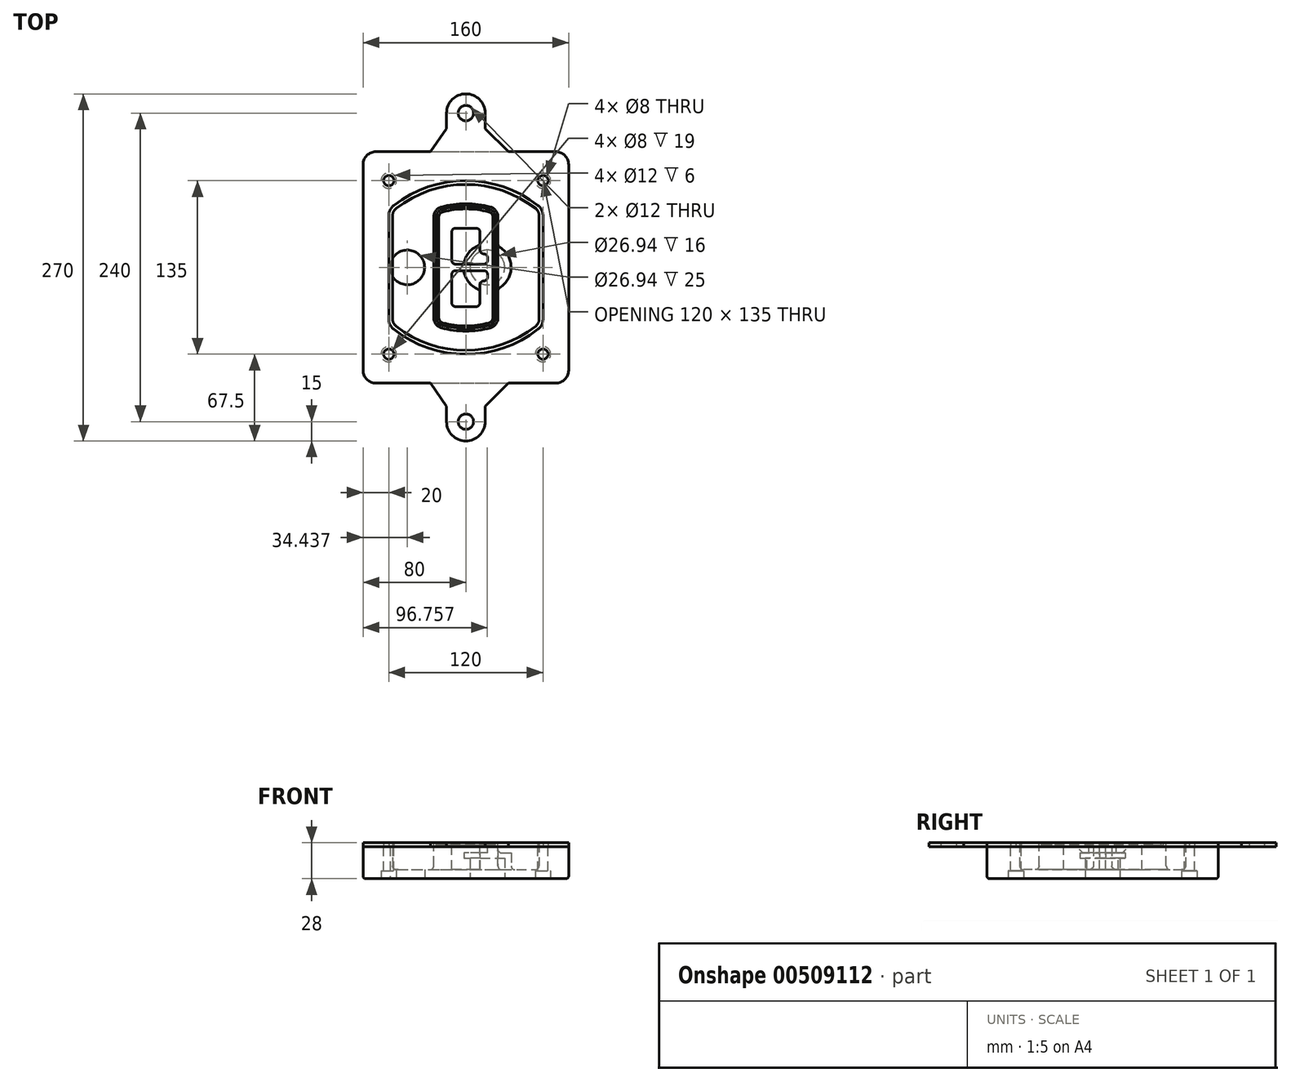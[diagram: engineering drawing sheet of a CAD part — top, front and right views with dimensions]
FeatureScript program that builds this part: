
annotation { "Feature Type Name" : "Feature", "Feature Type Description" : "" }
export const myFeature = defineFeature(function(context is Context, id is Id, definition is map)
    precondition{}
    {
        {
            var Q0;
            Q0=qCreatedBy(makeId("Top.planeOp"),FACE);
            var sketch = newSketch(context, id + "F0", { "sketchPlane" : qUnion([Q0])});
            skPoint(sketch, "E0.rect.middle", {"position": v(0, 0) * mm});
            skLineSegment(sketch, "E1.bottom", {"start": v(-70, -90) * mm, "end": v(70, -90) * mm});
            skLineSegment(sketch, "E1.top", {"start": v(-70, 90) * mm, "end": v(70, 90) * mm});
            skLineSegment(sketch, "E1.left", {"start": v(-80, -80) * mm, "end": v(-80, 80) * mm});
            skLineSegment(sketch, "E1.right", {"start": v(80, -80) * mm, "end": v(80, 80) * mm});
            skLineSegment(sketch, "E2", {"start": v(-80, 90) * mm, "end": v(80, -90) * mm, "construction": true});
            skLineSegment(sketch, "E3", {"start": v(80, 90) * mm, "end": v(-80, -90) * mm, "construction": true});
            skCircle(sketch, "E4", {"center": v(-60, 67.5) * mm, "radius": 4 * mm});
            skCircle(sketch, "E5", {"center": v(60, 67.5) * mm, "radius": 4 * mm});
            skCircle(sketch, "E6", {"center": v(60, -67.5) * mm, "radius": 4 * mm});
            skCircle(sketch, "E7", {"center": v(-60, -67.5) * mm, "radius": 4 * mm});
            skLineSegment(sketch, "E8", {"start": v(-60, 67.5) * mm, "end": v(60, 67.5) * mm, "construction": true});
            skLineSegment(sketch, "E9", {"start": v(60, 67.5) * mm, "end": v(60, -67.5) * mm, "construction": true});
            skLineSegment(sketch, "E10", {"start": v(60, -67.5) * mm, "end": v(-60, -67.5) * mm, "construction": true});
            skLineSegment(sketch, "E11", {"start": v(-60, -67.5) * mm, "end": v(-60, 67.5) * mm, "construction": true});
            skLineSegment(sketch, "E12", {"start": v(-60, 40.3) * mm, "end": v(-60, -40.3) * mm});
            skLineSegment(sketch, "E13", {"start": v(60, 40.3) * mm, "end": v(60, -40.3) * mm});
            skArc(sketch, "E14", {"start": v(56.15, 48.18) * mm, "mid": v(0, 67.5) * mm, "end": v(-56.15, 48.18) * mm});
            skArc(sketch, "E15", {"start": v(-56.15, -48.18) * mm, "mid": v(0, -67.5) * mm, "end": v(56.15, -48.18) * mm});
            skLineSegment(sketch, "E16", {"start": v(-60, 0) * mm, "end": v(60, 0) * mm, "construction": true});
            skPoint(sketch, "E17.visualSharp", {"position": v(-60, -45) * mm});
            skArc(sketch, "E17.filletArc", {"start": v(-60, -40.3) * mm, "mid": v(-58.99, -44.68) * mm, "end": v(-56.15, -48.18) * mm});
            skPoint(sketch, "E18.visualSharp", {"position": v(-60, 45) * mm});
            skArc(sketch, "E18.filletArc", {"start": v(-56.15, 48.18) * mm, "mid": v(-58.99, 44.68) * mm, "end": v(-60, 40.3) * mm});
            skPoint(sketch, "E19.visualSharp", {"position": v(60, 45) * mm});
            skArc(sketch, "E19.filletArc", {"start": v(60, 40.3) * mm, "mid": v(58.99, 44.68) * mm, "end": v(56.15, 48.18) * mm});
            skPoint(sketch, "E20.visualSharp", {"position": v(60, -45) * mm});
            skArc(sketch, "E20.filletArc", {"start": v(56.15, -48.18) * mm, "mid": v(58.99, -44.68) * mm, "end": v(60, -40.3) * mm});
            skPoint(sketch, "E21.visualSharp", {"position": v(-80, 90) * mm});
            skArc(sketch, "E21.filletArc", {"start": v(-70, 90) * mm, "mid": v(-77.07, 87.07) * mm, "end": v(-80, 80) * mm});
            skPoint(sketch, "E22.visualSharp", {"position": v(80, 90) * mm});
            skArc(sketch, "E22.filletArc", {"start": v(80, 80) * mm, "mid": v(77.07, 87.07) * mm, "end": v(70, 90) * mm});
            skPoint(sketch, "E23.visualSharp", {"position": v(80, -90) * mm});
            skArc(sketch, "E23.filletArc", {"start": v(70, -90) * mm, "mid": v(77.07, -87.07) * mm, "end": v(80, -80) * mm});
            skPoint(sketch, "E24.visualSharp", {"position": v(-80, -90) * mm});
            skArc(sketch, "E24.filletArc", {"start": v(-80, -80) * mm, "mid": v(-77.07, -87.07) * mm, "end": v(-70, -90) * mm});
            skArc(sketch, "E25.0", {"start": v(57, 40.3) * mm, "mid": v(56.3, 43.36) * mm, "end": v(54.3, 45.81) * mm});
            skLineSegment(sketch, "E25.1", {"start": v(57, 40.3) * mm, "end": v(57, -40.3) * mm});
            skArc(sketch, "E25.2", {"start": v(54.3, -45.81) * mm, "mid": v(56.3, -43.36) * mm, "end": v(57, -40.3) * mm});
            skArc(sketch, "E25.3", {"start": v(-54.3, -45.81) * mm, "mid": v(0, -64.5) * mm, "end": v(54.3, -45.81) * mm});
            skArc(sketch, "E25.4", {"start": v(-57, -40.3) * mm, "mid": v(-56.3, -43.36) * mm, "end": v(-54.3, -45.81) * mm});
            skArc(sketch, "E25.5", {"start": v(54.3, 45.81) * mm, "mid": v(0, 64.5) * mm, "end": v(-54.3, 45.81) * mm});
            skLineSegment(sketch, "E25.6", {"start": v(-57, 40.3) * mm, "end": v(-57, -40.3) * mm});
            skArc(sketch, "E25.7", {"start": v(-54.3, 45.81) * mm, "mid": v(-56.3, 43.36) * mm, "end": v(-57, 40.3) * mm});
            skArc(sketch, "E26.0", {"start": v(-58.62, 51.33) * mm, "mid": v(-62.58, 46.43) * mm, "end": v(-64, 40.3) * mm});
            skArc(sketch, "E26.1", {"start": v(58.62, 51.33) * mm, "mid": v(0, 71.5) * mm, "end": v(-58.62, 51.33) * mm});
            skArc(sketch, "E26.2", {"start": v(64, 40.3) * mm, "mid": v(62.58, 46.43) * mm, "end": v(58.62, 51.33) * mm});
            skLineSegment(sketch, "E26.3", {"start": v(64, 40.3) * mm, "end": v(64, -40.3) * mm});
            skArc(sketch, "E26.4", {"start": v(58.62, -51.33) * mm, "mid": v(62.58, -46.43) * mm, "end": v(64, -40.3) * mm});
            skLineSegment(sketch, "E26.5", {"start": v(-64, 40.3) * mm, "end": v(-64, -40.3) * mm});
            skArc(sketch, "E26.6", {"start": v(-58.62, -51.33) * mm, "mid": v(0, -71.5) * mm, "end": v(58.62, -51.33) * mm});
            skArc(sketch, "E26.7", {"start": v(-64, -40.3) * mm, "mid": v(-62.58, -46.43) * mm, "end": v(-58.62, -51.33) * mm});
            skSolve(sketch);
        }
        {
            var Q0;
            Q0=makeQuery(id+"F0.imprint","IMPRINT",FACE,{"disambiguationData":[TD([[makeQuery(id+"F0.imprint","IMPRINT",EDGE,{"derivedFrom":sQuery(id+"F0.wireOp",EDGE,"E1.bottom")}),1.0]])]});
            var Q1;
            Q1=makeQuery(id+"F0.imprint","IMPRINT",FACE,{"disambiguationData":[TD([[makeQuery(id+"F0.imprint","IMPRINT",EDGE,{"derivedFrom":sQuery(id+"F0.wireOp",EDGE,"E12")}),1.0]])]});
            var Q2;
            Q2=makeQuery(id+"F0.imprint","IMPRINT",FACE,{"disambiguationData":[TD([[makeQuery(id+"F0.imprint","IMPRINT",EDGE,{"derivedFrom":sQuery(id+"F0.wireOp",EDGE,"E25.0")}),1.0]])]});
            var Q3;
            Q3=makeQuery(id+"F0.imprint","IMPRINT",FACE,{"disambiguationData":[TD([[makeQuery(id+"F0.imprint","IMPRINT",EDGE,{"derivedFrom":sQuery(id+"F0.wireOp",EDGE,"E12")}),-1.0]])]});
            extrude(context, id + "F1", {"entities" : qUnion([Q0, Q1, Q2, Q3]), "oppositeDirection" : true, "depth" : 25 * mm});
        }
        {
            var Q0;
            Q0=makeQuery(id+"F0.imprint","IMPRINT",FACE,{"disambiguationData":[TD([[makeQuery(id+"F0.imprint","IMPRINT",EDGE,{"derivedFrom":sQuery(id+"F0.wireOp",EDGE,"E12")}),1.0]])]});
            extrude(context, id + "F2", {"entities" : qUnion([Q0]), "operationType" : NewBodyOperationType.ADD, "depth" : 3 * mm});
        }
        {
            var Q0;
            Q0=makeQuery(id+"F0.imprint","IMPRINT",FACE,{"disambiguationData":[TD([[makeQuery(id+"F0.imprint","IMPRINT",EDGE,{"derivedFrom":sQuery(id+"F0.wireOp",EDGE,"E25.0")}),1.0]])]});
            extrude(context, id + "F3", {"entities" : qUnion([Q0]), "operationType" : NewBodyOperationType.REMOVE, "oppositeDirection" : true, "depth" : 18 * mm});
        }
        {
            var Q0;
            Q0=makeQuery(id+"F2.opExtrude","CAP_FACE",FACE,{"disambiguationData":[OSD([sQuery(id+"F0.wireOp",EDGE,"E12"),sQuery(id+"F0.wireOp",EDGE,"E13"),sQuery(id+"F0.wireOp",EDGE,"E14"),sQuery(id+"F0.wireOp",EDGE,"E15"),sQuery(id+"F0.wireOp",EDGE,"E17.filletArc"),sQuery(id+"F0.wireOp",EDGE,"E18.filletArc"),sQuery(id+"F0.wireOp",EDGE,"E19.filletArc"),sQuery(id+"F0.wireOp",EDGE,"E20.filletArc"),sQuery(id+"F0.wireOp",EDGE,"E25.0"),sQuery(id+"F0.wireOp",EDGE,"E25.1"),sQuery(id+"F0.wireOp",EDGE,"E25.2"),sQuery(id+"F0.wireOp",EDGE,"E25.3"),sQuery(id+"F0.wireOp",EDGE,"E25.4"),sQuery(id+"F0.wireOp",EDGE,"E25.5"),sQuery(id+"F0.wireOp",EDGE,"E25.6"),sQuery(id+"F0.wireOp",EDGE,"E25.7")])],"isStart":false});
            var sketch = newSketch(context, id + "F4", { "sketchPlane" : qUnion([Q0])});
            skArc(sketch, "E27.0", {"start": v(-19.08, -46.97) * mm, "mid": v(0, -49.5) * mm, "end": v(19.08, -46.97) * mm});
            skArc(sketch, "E28.0", {"start": v(19.08, 46.97) * mm, "mid": v(0, 49.5) * mm, "end": v(-19.08, 46.97) * mm});
            skLineSegment(sketch, "E29", {"start": v(-25, 39.25) * mm, "end": v(-25, -39.25) * mm});
            skLineSegment(sketch, "E30", {"start": v(25, 39.25) * mm, "end": v(25, -39.25) * mm});
            skLineSegment(sketch, "E31", {"start": v(-25, 45.1) * mm, "end": v(25, 45.1) * mm, "construction": true});
            skLineSegment(sketch, "E32", {"start": v(-25, -45.1) * mm, "end": v(25, -45.1) * mm, "construction": true});
            skPoint(sketch, "E33.visualSharp", {"position": v(-25, 45.1) * mm});
            skArc(sketch, "E33.filletArc", {"start": v(-19.08, 46.97) * mm, "mid": v(-23.35, 44.11) * mm, "end": v(-25, 39.25) * mm});
            skPoint(sketch, "E34.visualSharp", {"position": v(25, 45.1) * mm});
            skArc(sketch, "E34.filletArc", {"start": v(25, 39.25) * mm, "mid": v(23.35, 44.11) * mm, "end": v(19.08, 46.97) * mm});
            skPoint(sketch, "E35.visualSharp", {"position": v(25, -45.1) * mm});
            skArc(sketch, "E35.filletArc", {"start": v(19.08, -46.97) * mm, "mid": v(23.35, -44.11) * mm, "end": v(25, -39.25) * mm});
            skPoint(sketch, "E36.visualSharp", {"position": v(-25, -45.1) * mm});
            skArc(sketch, "E36.filletArc", {"start": v(-25, -39.25) * mm, "mid": v(-23.35, -44.11) * mm, "end": v(-19.08, -46.97) * mm});
            skArc(sketch, "E37.0", {"start": v(54.3, 45.81) * mm, "mid": v(0, 64.5) * mm, "end": v(-54.3, 45.81) * mm});
            skArc(sketch, "E37.1", {"start": v(-54.3, 45.81) * mm, "mid": v(-56.3, 43.36) * mm, "end": v(-57, 40.3) * mm});
            skLineSegment(sketch, "E37.2", {"start": v(-57, 40.3) * mm, "end": v(-57, -40.3) * mm});
            skArc(sketch, "E37.3", {"start": v(-57, -40.3) * mm, "mid": v(-56.3, -43.36) * mm, "end": v(-54.3, -45.81) * mm});
            skArc(sketch, "E37.4", {"start": v(-54.3, -45.81) * mm, "mid": v(0, -64.5) * mm, "end": v(54.3, -45.81) * mm});
            skArc(sketch, "E37.5", {"start": v(54.3, -45.81) * mm, "mid": v(56.3, -43.36) * mm, "end": v(57, -40.3) * mm});
            skLineSegment(sketch, "E37.6", {"start": v(57, 40.3) * mm, "end": v(57, -40.3) * mm});
            skArc(sketch, "E37.7", {"start": v(57, 40.3) * mm, "mid": v(56.3, 43.36) * mm, "end": v(54.3, 45.81) * mm});
            skLineSegment(sketch, "E38.0", {"start": v(23, 39.25) * mm, "end": v(23, -39.25) * mm});
            skArc(sketch, "E38.1", {"start": v(18.56, -45.04) * mm, "mid": v(21.76, -42.9) * mm, "end": v(23, -39.25) * mm});
            skArc(sketch, "E38.2", {"start": v(-18.56, -45.04) * mm, "mid": v(0, -47.5) * mm, "end": v(18.56, -45.04) * mm});
            skArc(sketch, "E38.3", {"start": v(-23, -39.25) * mm, "mid": v(-21.76, -42.9) * mm, "end": v(-18.56, -45.04) * mm});
            skLineSegment(sketch, "E38.4", {"start": v(-23, 39.25) * mm, "end": v(-23, -39.25) * mm});
            skArc(sketch, "E38.5", {"start": v(23, 39.25) * mm, "mid": v(21.76, 42.9) * mm, "end": v(18.56, 45.04) * mm});
            skArc(sketch, "E38.6", {"start": v(-18.56, 45.04) * mm, "mid": v(-21.76, 42.9) * mm, "end": v(-23, 39.25) * mm});
            skArc(sketch, "E38.7", {"start": v(18.56, 45.04) * mm, "mid": v(0, 47.5) * mm, "end": v(-18.56, 45.04) * mm});
            skArc(sketch, "E39.0", {"start": v(21, 39.25) * mm, "mid": v(20.18, 41.68) * mm, "end": v(18.04, 43.1) * mm});
            skLineSegment(sketch, "E39.1", {"start": v(21, 39.25) * mm, "end": v(21, -39.25) * mm});
            skArc(sketch, "E39.2", {"start": v(18.04, -43.1) * mm, "mid": v(20.18, -41.68) * mm, "end": v(21, -39.25) * mm});
            skArc(sketch, "E39.3", {"start": v(-18.04, -43.1) * mm, "mid": v(0, -45.5) * mm, "end": v(18.04, -43.1) * mm});
            skArc(sketch, "E39.4", {"start": v(-21, -39.25) * mm, "mid": v(-20.18, -41.68) * mm, "end": v(-18.04, -43.1) * mm});
            skArc(sketch, "E39.5", {"start": v(18.04, 43.1) * mm, "mid": v(0, 45.5) * mm, "end": v(-18.04, 43.1) * mm});
            skLineSegment(sketch, "E39.6", {"start": v(-21, 39.25) * mm, "end": v(-21, -39.25) * mm});
            skArc(sketch, "E39.7", {"start": v(-18.04, 43.1) * mm, "mid": v(-20.18, 41.68) * mm, "end": v(-21, 39.25) * mm});
            skLineSegment(sketch, "E40", {"start": v(-25, 0) * mm, "end": v(25, 0) * mm, "construction": true});
            skLineSegment(sketch, "E41", {"start": v(-11, 5.5) * mm, "end": v(-11, 27.5) * mm});
            skLineSegment(sketch, "E42", {"start": v(-8, 30.5) * mm, "end": v(8, 30.5) * mm});
            skLineSegment(sketch, "E43", {"start": v(11, 27.5) * mm, "end": v(11, 13.5) * mm});
            skLineSegment(sketch, "E44", {"start": v(14, 10.5) * mm, "end": v(14, 10.5) * mm});
            skLineSegment(sketch, "E45", {"start": v(17, 7.5) * mm, "end": v(17, 5.5) * mm});
            skLineSegment(sketch, "E46", {"start": v(14, 2.5) * mm, "end": v(-8, 2.5) * mm});
            skPoint(sketch, "E47.visualSharp", {"position": v(-11, 30.5) * mm});
            skArc(sketch, "E47.filletArc", {"start": v(-8, 30.5) * mm, "mid": v(-10.12, 29.62) * mm, "end": v(-11, 27.5) * mm});
            skPoint(sketch, "E48.visualSharp", {"position": v(11, 30.5) * mm});
            skArc(sketch, "E48.filletArc", {"start": v(11, 27.5) * mm, "mid": v(10.12, 29.62) * mm, "end": v(8, 30.5) * mm});
            skPoint(sketch, "E49.visualSharp", {"position": v(11, 10.5) * mm});
            skArc(sketch, "E49.filletArc", {"start": v(11, 13.5) * mm, "mid": v(11.88, 11.38) * mm, "end": v(14, 10.5) * mm});
            skPoint(sketch, "E50.visualSharp", {"position": v(17, 10.5) * mm});
            skArc(sketch, "E50.filletArc", {"start": v(17, 7.5) * mm, "mid": v(16.12, 9.62) * mm, "end": v(14, 10.5) * mm});
            skPoint(sketch, "E51.visualSharp", {"position": v(17, 2.5) * mm});
            skArc(sketch, "E51.filletArc", {"start": v(14, 2.5) * mm, "mid": v(16.12, 3.38) * mm, "end": v(17, 5.5) * mm});
            skPoint(sketch, "E52.visualSharp", {"position": v(-11, 2.5) * mm});
            skArc(sketch, "E52.filletArc", {"start": v(-11, 5.5) * mm, "mid": v(-10.12, 3.38) * mm, "end": v(-8, 2.5) * mm});
            skLineSegment(sketch, "E53.0.MirrorCS", {"start": v(14, -2.5) * mm, "end": v(-8, -2.5) * mm});
            skArc(sketch, "E54.0.MirrorCS", {"start": v(-11, -5.5) * mm, "mid": v(-10.12, -3.38) * mm, "end": v(-8, -2.5) * mm});
            skLineSegment(sketch, "E55.0.MirrorCS", {"start": v(-11, -5.5) * mm, "end": v(-11, -27.5) * mm});
            skArc(sketch, "E56.0.MirrorCS", {"start": v(-8, -30.5) * mm, "mid": v(-10.12, -29.62) * mm, "end": v(-11, -27.5) * mm});
            skLineSegment(sketch, "E57.0.MirrorCS", {"start": v(-8, -30.5) * mm, "end": v(8, -30.5) * mm});
            skArc(sketch, "E58.0.MirrorCS", {"start": v(11, -27.5) * mm, "mid": v(10.12, -29.62) * mm, "end": v(8, -30.5) * mm});
            skLineSegment(sketch, "E59.0.MirrorCS", {"start": v(11, -27.5) * mm, "end": v(11, -13.5) * mm});
            skArc(sketch, "E60.0.MirrorCS", {"start": v(11, -13.5) * mm, "mid": v(11.88, -11.38) * mm, "end": v(14, -10.5) * mm});
            skArc(sketch, "E61.0.MirrorCS", {"start": v(17, -7.5) * mm, "mid": v(16.12, -9.62) * mm, "end": v(14, -10.5) * mm});
            skLineSegment(sketch, "E62.0.MirrorCS", {"start": v(17, -7.5) * mm, "end": v(17, -5.5) * mm});
            skArc(sketch, "E63.0.MirrorCS", {"start": v(14, -2.5) * mm, "mid": v(16.12, -3.38) * mm, "end": v(17, -5.5) * mm});
            skSolve(sketch);
        }
        {
            var Q0;
            Q0=makeQuery(id+"F4.imprint","IMPRINT",FACE,{"disambiguationData":[TD([[makeQuery(id+"F4.imprint","IMPRINT",EDGE,{"derivedFrom":sQuery(id+"F4.wireOp",EDGE,"E27.0")}),1.0]])]});
            var Q1;
            Q1=makeQuery(id+"F4.imprint","IMPRINT",FACE,{"disambiguationData":[TD([[makeQuery(id+"F4.imprint","IMPRINT",EDGE,{"derivedFrom":sQuery(id+"F4.wireOp",EDGE,"E38.0")}),-1.0]])]});
            var Q2;
            Q2=makeQuery(id+"F4.imprint","IMPRINT",FACE,{"disambiguationData":[TD([[makeQuery(id+"F4.imprint","IMPRINT",EDGE,{"derivedFrom":sQuery(id+"F4.wireOp",EDGE,"E39.0")}),1.0]])]});
            extrude(context, id + "F5", {"entities" : qUnion([Q0, Q1, Q2]), "operationType" : NewBodyOperationType.ADD, "endBound" : BoundingType.UP_TO_NEXT, "oppositeDirection" : true, "depth" : 25 * mm});
        }
        {
            var Q0;
            Q0=makeQuery(id+"F4.imprint","IMPRINT",FACE,{"disambiguationData":[TD([[makeQuery(id+"F4.imprint","IMPRINT",EDGE,{"derivedFrom":sQuery(id+"F4.wireOp",EDGE,"E38.0")}),-1.0]])]});
            extrude(context, id + "F6", {"entities" : qUnion([Q0]), "operationType" : NewBodyOperationType.REMOVE, "oppositeDirection" : true, "depth" : 2 * mm});
        }
        {
            var Q0;
            Q0=makeQuery(id+"F1.opExtrude","CAP_FACE",FACE,{"disambiguationData":[OSD([sQuery(id+"F0.wireOp",EDGE,"E1.bottom"),sQuery(id+"F0.wireOp",EDGE,"E1.top"),sQuery(id+"F0.wireOp",EDGE,"E1.left"),sQuery(id+"F0.wireOp",EDGE,"E1.right"),sQuery(id+"F0.wireOp",EDGE,"E4"),sQuery(id+"F0.wireOp",EDGE,"E5"),sQuery(id+"F0.wireOp",EDGE,"E6"),sQuery(id+"F0.wireOp",EDGE,"E7"),sQuery(id+"F0.wireOp",EDGE,"E21.filletArc"),sQuery(id+"F0.wireOp",EDGE,"E22.filletArc"),sQuery(id+"F0.wireOp",EDGE,"E23.filletArc"),sQuery(id+"F0.wireOp",EDGE,"E24.filletArc")])],"isStart":false});
            var sketch = newSketch(context, id + "F7", { "sketchPlane" : qUnion([Q0])});
            skCircle(sketch, "E64", {"center": v(16.76, 0) * mm, "radius": 13.47 * mm});
            skCircle(sketch, "E65", {"center": v(-45.56, 0) * mm, "radius": 13.47 * mm});
            skLineSegment(sketch, "E66", {"start": v(80, 0) * mm, "end": v(-80, 0) * mm});
            skCircle(sketch, "E67", {"center": v(16.76, 0) * mm, "radius": 18.47 * mm});
            skCircle(sketch, "E68", {"center": v(60, -67.5) * mm, "radius": 6 * mm});
            skCircle(sketch, "E69", {"center": v(-60, -67.5) * mm, "radius": 6 * mm});
            skCircle(sketch, "E70", {"center": v(-60, 67.5) * mm, "radius": 6 * mm});
            skCircle(sketch, "E71", {"center": v(60, 67.5) * mm, "radius": 6 * mm});
            skSolve(sketch);
        }
        {
            var Q0;
            {var subQ1=sQuery(id+"F7.wireOp",EDGE,"E66");var subQ4=sQuery(id+"F7.wireOp",EDGE,"E64");var subQ6=makeQuery(id+"F7.imprint","INTERSECT",VERTEX,{"disambiguationData":[OD(0.0)],"derivedFrom":[subQ4,subQ1]});Q0=makeQuery(id+"F7.imprint","IMPRINT",FACE,{"disambiguationData":[TD([[makeQuery(id+"F7.imprint","IMPRINT",EDGE,{"disambiguationData":[TD([[subQ6,-1.0]])],"derivedFrom":subQ4}),-1.0]])]});}
            var Q1;
            {var subQ0=sQuery(id+"F7.wireOp",EDGE,"E66");var subQ1=sQuery(id+"F7.wireOp",EDGE,"E64");var subQ3=makeQuery(id+"F7.imprint","INTERSECT",VERTEX,{"disambiguationData":[OD(0.0)],"derivedFrom":[subQ1,subQ0]});Q1=makeQuery(id+"F7.imprint","IMPRINT",FACE,{"disambiguationData":[TD([[makeQuery(id+"F7.imprint","IMPRINT",EDGE,{"disambiguationData":[TD([[subQ3,-1.0]])],"derivedFrom":subQ1}),1.0]])]});}
            var Q2;
            {var subQ0=sQuery(id+"F7.wireOp",EDGE,"E66");var subQ1=sQuery(id+"F7.wireOp",EDGE,"E64");var subQ3=makeQuery(id+"F7.imprint","INTERSECT",VERTEX,{"disambiguationData":[OD(0.0)],"derivedFrom":[subQ1,subQ0]});Q2=makeQuery(id+"F7.imprint","IMPRINT",FACE,{"disambiguationData":[TD([[makeQuery(id+"F7.imprint","IMPRINT",EDGE,{"disambiguationData":[TD([[subQ3,1.0]])],"derivedFrom":subQ1}),1.0]])]});}
            var Q3;
            {var subQ1=sQuery(id+"F7.wireOp",EDGE,"E66");var subQ4=sQuery(id+"F7.wireOp",EDGE,"E64");var subQ6=makeQuery(id+"F7.imprint","INTERSECT",VERTEX,{"disambiguationData":[OD(0.0)],"derivedFrom":[subQ4,subQ1]});Q3=makeQuery(id+"F7.imprint","IMPRINT",FACE,{"disambiguationData":[TD([[makeQuery(id+"F7.imprint","IMPRINT",EDGE,{"disambiguationData":[TD([[subQ6,1.0]])],"derivedFrom":subQ4}),-1.0]])]});}
            extrude(context, id + "F8", {"entities" : qUnion([Q0, Q1, Q2, Q3]), "operationType" : NewBodyOperationType.ADD, "oppositeDirection" : true, "depth" : 20 * mm});
        }
        {
            var Q0;
            {var subQ0=sQuery(id+"F7.wireOp",EDGE,"E66");var subQ1=sQuery(id+"F7.wireOp",EDGE,"E64");var subQ3=makeQuery(id+"F7.imprint","INTERSECT",VERTEX,{"disambiguationData":[OD(0.0)],"derivedFrom":[subQ1,subQ0]});Q0=makeQuery(id+"F7.imprint","IMPRINT",FACE,{"disambiguationData":[TD([[makeQuery(id+"F7.imprint","IMPRINT",EDGE,{"disambiguationData":[TD([[subQ3,-1.0]])],"derivedFrom":subQ1}),1.0]])]});}
            var Q1;
            {var subQ0=sQuery(id+"F7.wireOp",EDGE,"E66");var subQ1=sQuery(id+"F7.wireOp",EDGE,"E64");var subQ3=makeQuery(id+"F7.imprint","INTERSECT",VERTEX,{"disambiguationData":[OD(0.0)],"derivedFrom":[subQ1,subQ0]});Q1=makeQuery(id+"F7.imprint","IMPRINT",FACE,{"disambiguationData":[TD([[makeQuery(id+"F7.imprint","IMPRINT",EDGE,{"disambiguationData":[TD([[subQ3,1.0]])],"derivedFrom":subQ1}),1.0]])]});}
            extrude(context, id + "F9", {"entities" : qUnion([Q0, Q1]), "operationType" : NewBodyOperationType.REMOVE, "oppositeDirection" : true, "depth" : 16 * mm});
        }
        {
            var Q0;
            {var subQ0=sQuery(id+"F7.wireOp",EDGE,"E66");var subQ1=sQuery(id+"F7.wireOp",EDGE,"E65");var subQ3=makeQuery(id+"F7.imprint","INTERSECT",VERTEX,{"disambiguationData":[OD(0.0)],"derivedFrom":[subQ1,subQ0]});Q0=makeQuery(id+"F7.imprint","IMPRINT",FACE,{"disambiguationData":[TD([[makeQuery(id+"F7.imprint","IMPRINT",EDGE,{"disambiguationData":[TD([[subQ3,-1.0]])],"derivedFrom":subQ1}),1.0]])]});}
            var Q1;
            {var subQ0=sQuery(id+"F7.wireOp",EDGE,"E66");var subQ1=sQuery(id+"F7.wireOp",EDGE,"E65");var subQ3=makeQuery(id+"F7.imprint","INTERSECT",VERTEX,{"disambiguationData":[OD(0.0)],"derivedFrom":[subQ1,subQ0]});Q1=makeQuery(id+"F7.imprint","IMPRINT",FACE,{"disambiguationData":[TD([[makeQuery(id+"F7.imprint","IMPRINT",EDGE,{"disambiguationData":[TD([[subQ3,1.0]])],"derivedFrom":subQ1}),1.0]])]});}
            extrude(context, id + "F10", {"entities" : qUnion([Q0, Q1]), "operationType" : NewBodyOperationType.REMOVE, "oppositeDirection" : true, "depth" : 25 * mm});
        }
        {
            var Q0;
            Q0=makeQuery(id+"F7.imprint","IMPRINT",FACE,{"disambiguationData":[TD([[makeQuery(id+"F7.imprint","IMPRINT",EDGE,{"derivedFrom":sQuery(id+"F7.wireOp",EDGE,"E68")}),1.0]])]});
            var Q1;
            Q1=makeQuery(id+"F7.imprint","IMPRINT",FACE,{"disambiguationData":[TD([[makeQuery(id+"F7.imprint","IMPRINT",EDGE,{"derivedFrom":makeQuery(id+"F1.opExtrude","CAP_EDGE",EDGE,{"disambiguationData":[OSD([sQuery(id+"F0.wireOp",EDGE,"E5")])],"isStart":false})}),-1.0]])]});
            var Q2;
            Q2=makeQuery(id+"F7.imprint","IMPRINT",FACE,{"disambiguationData":[TD([[makeQuery(id+"F7.imprint","IMPRINT",EDGE,{"derivedFrom":sQuery(id+"F7.wireOp",EDGE,"E69")}),1.0]])]});
            var Q3;
            Q3=makeQuery(id+"F7.imprint","IMPRINT",FACE,{"disambiguationData":[TD([[makeQuery(id+"F7.imprint","IMPRINT",EDGE,{"derivedFrom":makeQuery(id+"F1.opExtrude","CAP_EDGE",EDGE,{"disambiguationData":[OSD([sQuery(id+"F0.wireOp",EDGE,"E4")])],"isStart":false})}),-1.0]])]});
            var Q4;
            Q4=makeQuery(id+"F7.imprint","IMPRINT",FACE,{"disambiguationData":[TD([[makeQuery(id+"F7.imprint","IMPRINT",EDGE,{"derivedFrom":sQuery(id+"F7.wireOp",EDGE,"E70")}),1.0]])]});
            var Q5;
            Q5=makeQuery(id+"F7.imprint","IMPRINT",FACE,{"disambiguationData":[TD([[makeQuery(id+"F7.imprint","IMPRINT",EDGE,{"derivedFrom":makeQuery(id+"F1.opExtrude","CAP_EDGE",EDGE,{"disambiguationData":[OSD([sQuery(id+"F0.wireOp",EDGE,"E7")])],"isStart":false})}),-1.0]])]});
            var Q6;
            Q6=makeQuery(id+"F7.imprint","IMPRINT",FACE,{"disambiguationData":[TD([[makeQuery(id+"F7.imprint","IMPRINT",EDGE,{"derivedFrom":sQuery(id+"F7.wireOp",EDGE,"E71")}),1.0]])]});
            var Q7;
            Q7=makeQuery(id+"F7.imprint","IMPRINT",FACE,{"disambiguationData":[TD([[makeQuery(id+"F7.imprint","IMPRINT",EDGE,{"derivedFrom":makeQuery(id+"F1.opExtrude","CAP_EDGE",EDGE,{"disambiguationData":[OSD([sQuery(id+"F0.wireOp",EDGE,"E6")])],"isStart":false})}),-1.0]])]});
            extrude(context, id + "F11", {"entities" : qUnion([Q0, Q1, Q2, Q3, Q4, Q5, Q6, Q7]), "operationType" : NewBodyOperationType.REMOVE, "oppositeDirection" : true, "depth" : 6 * mm});
        }
        {
            var Q0;
            Q0=makeQuery(id+"F9.boolean.opBoolean","COPY",FACE,{"derivedFrom":makeQuery(id+"F9.opExtrude","CAP_FACE",FACE,{"disambiguationData":[OSD([sQuery(id+"F7.wireOp",EDGE,"E64")])],"isStart":false})});
            var sketch = newSketch(context, id + "F12", { "sketchPlane" : qUnion([Q0])});
            skArc(sketch, "E72.0", {"start": v(11, 17.55) * mm, "mid": v(2.57, 11.82) * mm, "end": v(-1.54, 2.5) * mm});
            skArc(sketch, "E72.1", {"start": v(-1.54, -2.5) * mm, "mid": v(2.57, -11.82) * mm, "end": v(11, -17.55) * mm});
            skLineSegment(sketch, "E73", {"start": v(-1.54, -2.5) * mm, "end": v(14, -2.5) * mm});
            skLineSegment(sketch, "E74.0", {"start": v(14, 2.5) * mm, "end": v(-1.54, 2.5) * mm});
            skArc(sketch, "E74.1", {"start": v(14, 2.5) * mm, "mid": v(16.12, 3.38) * mm, "end": v(17, 5.5) * mm});
            skLineSegment(sketch, "E74.2", {"start": v(17, 7.5) * mm, "end": v(17, 5.5) * mm});
            skArc(sketch, "E74.3", {"start": v(17, 7.5) * mm, "mid": v(16.12, 9.62) * mm, "end": v(14, 10.5) * mm});
            skArc(sketch, "E74.4", {"start": v(11, 13.5) * mm, "mid": v(11.88, 11.38) * mm, "end": v(14, 10.5) * mm});
            skLineSegment(sketch, "E74.5", {"start": v(11, 17.55) * mm, "end": v(11, 13.5) * mm});
            skLineSegment(sketch, "E74.7", {"start": v(14, -2.5) * mm, "end": v(-1.54, -2.5) * mm});
            skArc(sketch, "E74.8", {"start": v(14, -2.5) * mm, "mid": v(16.12, -3.38) * mm, "end": v(17, -5.5) * mm});
            skLineSegment(sketch, "E74.9", {"start": v(17, -7.5) * mm, "end": v(17, -5.5) * mm});
            skArc(sketch, "E74.10", {"start": v(17, -7.5) * mm, "mid": v(16.12, -9.62) * mm, "end": v(14, -10.5) * mm});
            skArc(sketch, "E74.11", {"start": v(11, -13.5) * mm, "mid": v(11.88, -11.38) * mm, "end": v(14, -10.5) * mm});
            skLineSegment(sketch, "E74.12", {"start": v(11, -17.55) * mm, "end": v(11, -13.5) * mm});
            skPoint(sketch, "E75.orphan", {"position": v(11, -27.5) * mm});
            skPoint(sketch, "E76.orphan", {"position": v(-8, -2.5) * mm});
            skPoint(sketch, "E77.orphan", {"position": v(-8, 2.5) * mm});
            skPoint(sketch, "E78.orphan", {"position": v(11, 27.5) * mm});
            skSolve(sketch);
        }
        {
            var Q0;
            {var subQ7=sQuery(id+"F12.wireOp",EDGE,"E72.0");var subQ14=sQuery(id+"F12.wireOp",EDGE,"E72.1");var subQ16=sQuery(id+"F12.wireOp",EDGE,"E74.1");var subQ18=sQuery(id+"F12.wireOp",EDGE,"E74.8");Q0=qUnion([makeQuery(id+"F12.imprint","IMPRINT",FACE,{"disambiguationData":[TD([[makeQuery(id+"F12.imprint","IMPRINT",EDGE,{"derivedFrom":subQ7}),1.0]])]}),makeQuery(id+"F12.imprint","IMPRINT",FACE,{"disambiguationData":[TD([[makeQuery(id+"F12.imprint","IMPRINT",EDGE,{"derivedFrom":subQ14}),1.0]])]}),makeQuery(id+"F12.imprint","IMPRINT",FACE,{"disambiguationData":[TD([[makeQuery(id+"F12.imprint","IMPRINT",EDGE,{"derivedFrom":subQ16}),1.0]])]}),makeQuery(id+"F12.imprint","IMPRINT",FACE,{"disambiguationData":[TD([[makeQuery(id+"F12.imprint","IMPRINT",EDGE,{"derivedFrom":subQ18}),-1.0]])]})]);}
            var Q1;
            Q1=makeQuery(id+"F5.boolean.opBoolean","SPLIT",FACE,{"disambiguationData":[TD([makeQuery(id+"F5.opExtrude","SWEPT_FACE",FACE,{"disambiguationData":[OSD([sQuery(id+"F4.wireOp",EDGE,"E41")])]})])],"derivedFrom":makeQuery(id+"F3.boolean.opBoolean","COPY",FACE,{"derivedFrom":makeQuery(id+"F3.opExtrude","CAP_FACE",FACE,{"disambiguationData":[OSD([sQuery(id+"F0.wireOp",EDGE,"E25.0"),sQuery(id+"F0.wireOp",EDGE,"E25.1"),sQuery(id+"F0.wireOp",EDGE,"E25.2"),sQuery(id+"F0.wireOp",EDGE,"E25.3"),sQuery(id+"F0.wireOp",EDGE,"E25.4"),sQuery(id+"F0.wireOp",EDGE,"E25.5"),sQuery(id+"F0.wireOp",EDGE,"E25.6"),sQuery(id+"F0.wireOp",EDGE,"E25.7")])],"isStart":false})})});
            extrude(context, id + "F13", {"entities" : qUnion([Q0]), "operationType" : NewBodyOperationType.REMOVE, "endBound" : BoundingType.UP_TO_SURFACE, "endBoundEntityFace" : qUnion([Q1]), "depth" : 25 * mm});
        }
        {
            var Q0;
            Q0=makeQuery(id+"F3.boolean.opBoolean","COPY",EDGE,{"derivedFrom":makeQuery(id+"F3.opExtrude","CAP_EDGE",EDGE,{"disambiguationData":[OSD([sQuery(id+"F0.wireOp",EDGE,"E25.6")])],"isStart":false})});
            var Q1;
            Q1=makeQuery(id+"F8.boolean.opBoolean","INTERSECT",EDGE,{"derivedFrom":[makeQuery(id+"F5.opExtrude","SWEPT_FACE",FACE,{"disambiguationData":[OSD([sQuery(id+"F4.wireOp",EDGE,"E30")])]}),makeQuery(id+"F8.opExtrude","CAP_FACE",FACE,{"disambiguationData":[OSD([sQuery(id+"F7.wireOp",EDGE,"E67")])],"isStart":false})]});
            var Q2;
            Q2=makeQuery(id+"F8.boolean.opBoolean","INTERSECT",EDGE,{"disambiguationData":[OD(1.0)],"derivedFrom":[makeQuery(id+"F5.opExtrude","SWEPT_FACE",FACE,{"disambiguationData":[OSD([sQuery(id+"F4.wireOp",EDGE,"E30")])]}),makeQuery(id+"F8.opExtrude","SWEPT_FACE",FACE,{"disambiguationData":[OSD([sQuery(id+"F7.wireOp",EDGE,"E67")])]})]});
            var Q3;
            {var subQ0=sQuery(id+"F4.wireOp",EDGE,"E30");Q3=makeQuery(id+"F8.boolean.opBoolean","SPLIT",EDGE,{"disambiguationData":[TD([makeQuery(id+"F5.opExtrude","SWEPT_FACE",FACE,{"disambiguationData":[OSD([sQuery(id+"F4.wireOp",EDGE,"E35.filletArc")])]})])],"derivedFrom":makeQuery(id+"F5.opExtrude","CAP_EDGE",EDGE,{"disambiguationData":[OSD([subQ0])],"isStart":false})});}
            var Q4;
            {var subQ0=sQuery(id+"F0.wireOp",EDGE,"E25.7");var subQ1=sQuery(id+"F0.wireOp",EDGE,"E25.1");var subQ2=sQuery(id+"F0.wireOp",EDGE,"E25.6");var subQ3=sQuery(id+"F0.wireOp",EDGE,"E25.5");var subQ4=sQuery(id+"F0.wireOp",EDGE,"E25.4");var subQ5=sQuery(id+"F0.wireOp",EDGE,"E25.0");var subQ6=sQuery(id+"F0.wireOp",EDGE,"E25.2");var subQ7=sQuery(id+"F0.wireOp",EDGE,"E25.3");Q4=makeQuery(id+"F8.boolean.opBoolean","INTERSECT",EDGE,{"derivedFrom":[makeQuery(id+"F5.boolean.opBoolean","SPLIT",FACE,{"disambiguationData":[TD([makeQuery(id+"F2.opExtrude","SWEPT_FACE",FACE,{"disambiguationData":[OSD([subQ5])]})])],"derivedFrom":makeQuery(id+"F3.boolean.opBoolean","COPY",FACE,{"derivedFrom":makeQuery(id+"F3.opExtrude","CAP_FACE",FACE,{"disambiguationData":[OSD([subQ5,subQ1,subQ6,subQ7,subQ4,subQ3,subQ2,subQ0])],"isStart":false})})}),makeQuery(id+"F8.opExtrude","SWEPT_FACE",FACE,{"disambiguationData":[OSD([sQuery(id+"F7.wireOp",EDGE,"E67")])]})]});}
            var Q5;
            Q5=makeQuery(id+"F8.boolean.opBoolean","INTERSECT",EDGE,{"disambiguationData":[OD(0.0)],"derivedFrom":[makeQuery(id+"F5.opExtrude","SWEPT_FACE",FACE,{"disambiguationData":[OSD([sQuery(id+"F4.wireOp",EDGE,"E30")])]}),makeQuery(id+"F8.opExtrude","SWEPT_FACE",FACE,{"disambiguationData":[OSD([sQuery(id+"F7.wireOp",EDGE,"E67")])]})]});
            fillet(context, id + "F14", {"entities" : qUnion([Q0, Q1, Q2, Q3, Q4, Q5]), "radius" : 3 * mm, "tangentPropagation" : true, "allowEdgeOverflow" : false});
        }
        {
            var Q0;
            Q0=makeQuery(id+"F1.opExtrude","CAP_EDGE",EDGE,{"disambiguationData":[OSD([sQuery(id+"F0.wireOp",EDGE,"E1.bottom")])],"isStart":false});
            fillet(context, id + "F15", {"entities" : qUnion([Q0]), "radius" : 2 * mm, "tangentPropagation" : true, "allowEdgeOverflow" : false});
        }
        {
            var Q0;
            {var subQ0=sQuery(id+"F0.wireOp",EDGE,"E21.filletArc");var subQ1=sQuery(id+"F0.wireOp",EDGE,"E7");var subQ2=sQuery(id+"F0.wireOp",EDGE,"E6");var subQ3=sQuery(id+"F0.wireOp",EDGE,"E5");var subQ4=sQuery(id+"F0.wireOp",EDGE,"E4");var subQ5=sQuery(id+"F0.wireOp",EDGE,"E22.filletArc");var subQ6=sQuery(id+"F0.wireOp",EDGE,"E1.bottom");var subQ7=sQuery(id+"F0.wireOp",EDGE,"E1.right");var subQ8=sQuery(id+"F0.wireOp",EDGE,"E1.top");var subQ9=sQuery(id+"F0.wireOp",EDGE,"E1.left");var subQ10=sQuery(id+"F0.wireOp",EDGE,"E23.filletArc");var subQ11=sQuery(id+"F0.wireOp",EDGE,"E24.filletArc");Q0=makeQuery(id+"F2.boolean.opBoolean","SPLIT",FACE,{"disambiguationData":[TD([makeQuery(id+"F1.opExtrude","SWEPT_FACE",FACE,{"disambiguationData":[OSD([subQ6])]})])],"derivedFrom":makeQuery(id+"F1.opExtrude","CAP_FACE",FACE,{"disambiguationData":[OSD([subQ6,subQ8,subQ9,subQ7,subQ4,subQ3,subQ2,subQ1,subQ0,subQ5,subQ10,subQ11])],"isStart":true})});}
            var sketch = newSketch(context, id + "F16", { "sketchPlane" : qUnion([Q0])});
            skLineSegment(sketch, "E79.0", {"start": v(-70, 90) * mm, "end": v(70, 90) * mm});
            skLineSegment(sketch, "E79.1", {"start": v(-80, -80) * mm, "end": v(-80, 80) * mm});
            skLineSegment(sketch, "E79.2", {"start": v(-70, -90) * mm, "end": v(70, -90) * mm});
            skLineSegment(sketch, "E79.3", {"start": v(80, -80) * mm, "end": v(80, 80) * mm});
            skArc(sketch, "E79.4", {"start": v(80, 80) * mm, "mid": v(77.07, 87.07) * mm, "end": v(70, 90) * mm});
            skArc(sketch, "E79.5", {"start": v(-70, 90) * mm, "mid": v(-77.07, 87.07) * mm, "end": v(-80, 80) * mm});
            skArc(sketch, "E79.6", {"start": v(-80, -80) * mm, "mid": v(-77.07, -87.07) * mm, "end": v(-70, -90) * mm});
            skArc(sketch, "E79.7", {"start": v(70, -90) * mm, "mid": v(77.07, -87.07) * mm, "end": v(80, -80) * mm});
            skCircle(sketch, "E79.8", {"center": v(-60, 67.5) * mm, "radius": 4 * mm});
            skCircle(sketch, "E79.9", {"center": v(60, 67.5) * mm, "radius": 4 * mm});
            skCircle(sketch, "E79.10", {"center": v(-60, -67.5) * mm, "radius": 4 * mm});
            skCircle(sketch, "E79.11", {"center": v(60, -67.5) * mm, "radius": 4 * mm});
            skLineSegment(sketch, "E79.12", {"start": v(-60, 40.3) * mm, "end": v(-60, -40.3) * mm});
            skArc(sketch, "E79.13", {"start": v(56.15, 48.18) * mm, "mid": v(0, 67.5) * mm, "end": v(-56.15, 48.18) * mm});
            skArc(sketch, "E79.14", {"start": v(-56.15, 48.18) * mm, "mid": v(-58.99, 44.68) * mm, "end": v(-60, 40.3) * mm});
            skArc(sketch, "E79.15", {"start": v(-56.15, -48.18) * mm, "mid": v(0, -67.5) * mm, "end": v(56.15, -48.18) * mm});
            skArc(sketch, "E79.16", {"start": v(-60, -40.3) * mm, "mid": v(-58.99, -44.68) * mm, "end": v(-56.15, -48.18) * mm});
            skLineSegment(sketch, "E79.17", {"start": v(60, 40.3) * mm, "end": v(60, -40.3) * mm});
            skArc(sketch, "E79.18", {"start": v(56.15, -48.18) * mm, "mid": v(58.99, -44.68) * mm, "end": v(60, -40.3) * mm});
            skArc(sketch, "E79.19", {"start": v(60, 40.3) * mm, "mid": v(58.99, 44.68) * mm, "end": v(56.15, 48.18) * mm});
            skLineSegment(sketch, "E80", {"start": v(0, 90) * mm, "end": v(0, 120) * mm, "construction": true});
            skPoint(sketch, "E80.endSnap0", {"position": v(0, 90) * mm});
            skLineSegment(sketch, "E81", {"start": v(-27.44, 90) * mm, "end": v(-15, 108) * mm});
            skLineSegment(sketch, "E82", {"start": v(-15, 108) * mm, "end": v(-15, 120) * mm});
            skLineSegment(sketch, "E83", {"start": v(33, 90) * mm, "end": v(15, 108) * mm});
            skLineSegment(sketch, "E84", {"start": v(15, 108) * mm, "end": v(15, 120) * mm});
            skArc(sketch, "E85", {"start": v(-15, 120) * mm, "mid": v(0, 135) * mm, "end": v(15, 120) * mm});
            skCircle(sketch, "E86", {"center": v(0, 120) * mm, "radius": 6 * mm});
            skLineSegment(sketch, "E87.MirrorCS", {"start": v(-70, 270) * mm, "end": v(70, 270) * mm});
            skLineSegment(sketch, "E88", {"start": v(80, 0) * mm, "end": v(-78.28, 0) * mm, "construction": true});
            skPoint(sketch, "E88.endSnap0", {"position": v(-80, 0) * mm});
            skCircle(sketch, "E89.MirrorC", {"center": v(0, -120) * mm, "radius": 6 * mm});
            skArc(sketch, "E90.MirrorCS", {"start": v(-15, -120) * mm, "mid": v(0, -135) * mm, "end": v(15, -120) * mm});
            skLineSegment(sketch, "E91.MirrorCS", {"start": v(15, -108) * mm, "end": v(15, -120) * mm});
            skLineSegment(sketch, "E92.MirrorCS", {"start": v(33, -90) * mm, "end": v(15, -108) * mm});
            skLineSegment(sketch, "E93.MirrorCS", {"start": v(-15, -108) * mm, "end": v(-15, -120) * mm});
            skLineSegment(sketch, "E94.MirrorCS", {"start": v(-27.44, -90) * mm, "end": v(-15, -108) * mm});
            skLineSegment(sketch, "E95.MirrorCS", {"start": v(0, -90) * mm, "end": v(0, -120) * mm, "construction": true});
            skSolve(sketch);
        }
        {
            var Q0;
            Q0 = qSketchRegion(id + "F16", true);
            var Q1;
            Q1=makeQuery(id+"F2.opExtrude","CAP_FACE",FACE,{"disambiguationData":[OSD([sQuery(id+"F0.wireOp",EDGE,"E12"),sQuery(id+"F0.wireOp",EDGE,"E13"),sQuery(id+"F0.wireOp",EDGE,"E14"),sQuery(id+"F0.wireOp",EDGE,"E15"),sQuery(id+"F0.wireOp",EDGE,"E17.filletArc"),sQuery(id+"F0.wireOp",EDGE,"E18.filletArc"),sQuery(id+"F0.wireOp",EDGE,"E19.filletArc"),sQuery(id+"F0.wireOp",EDGE,"E20.filletArc"),sQuery(id+"F0.wireOp",EDGE,"E25.0"),sQuery(id+"F0.wireOp",EDGE,"E25.1"),sQuery(id+"F0.wireOp",EDGE,"E25.2"),sQuery(id+"F0.wireOp",EDGE,"E25.3"),sQuery(id+"F0.wireOp",EDGE,"E25.4"),sQuery(id+"F0.wireOp",EDGE,"E25.5"),sQuery(id+"F0.wireOp",EDGE,"E25.6"),sQuery(id+"F0.wireOp",EDGE,"E25.7")])],"isStart":false});
            extrude(context, id + "F17", {"entities" : qUnion([Q0]), "endBound" : BoundingType.UP_TO_SURFACE, "endBoundEntityFace" : qUnion([Q1]), "depth" : 25 * mm});
        }
    });
